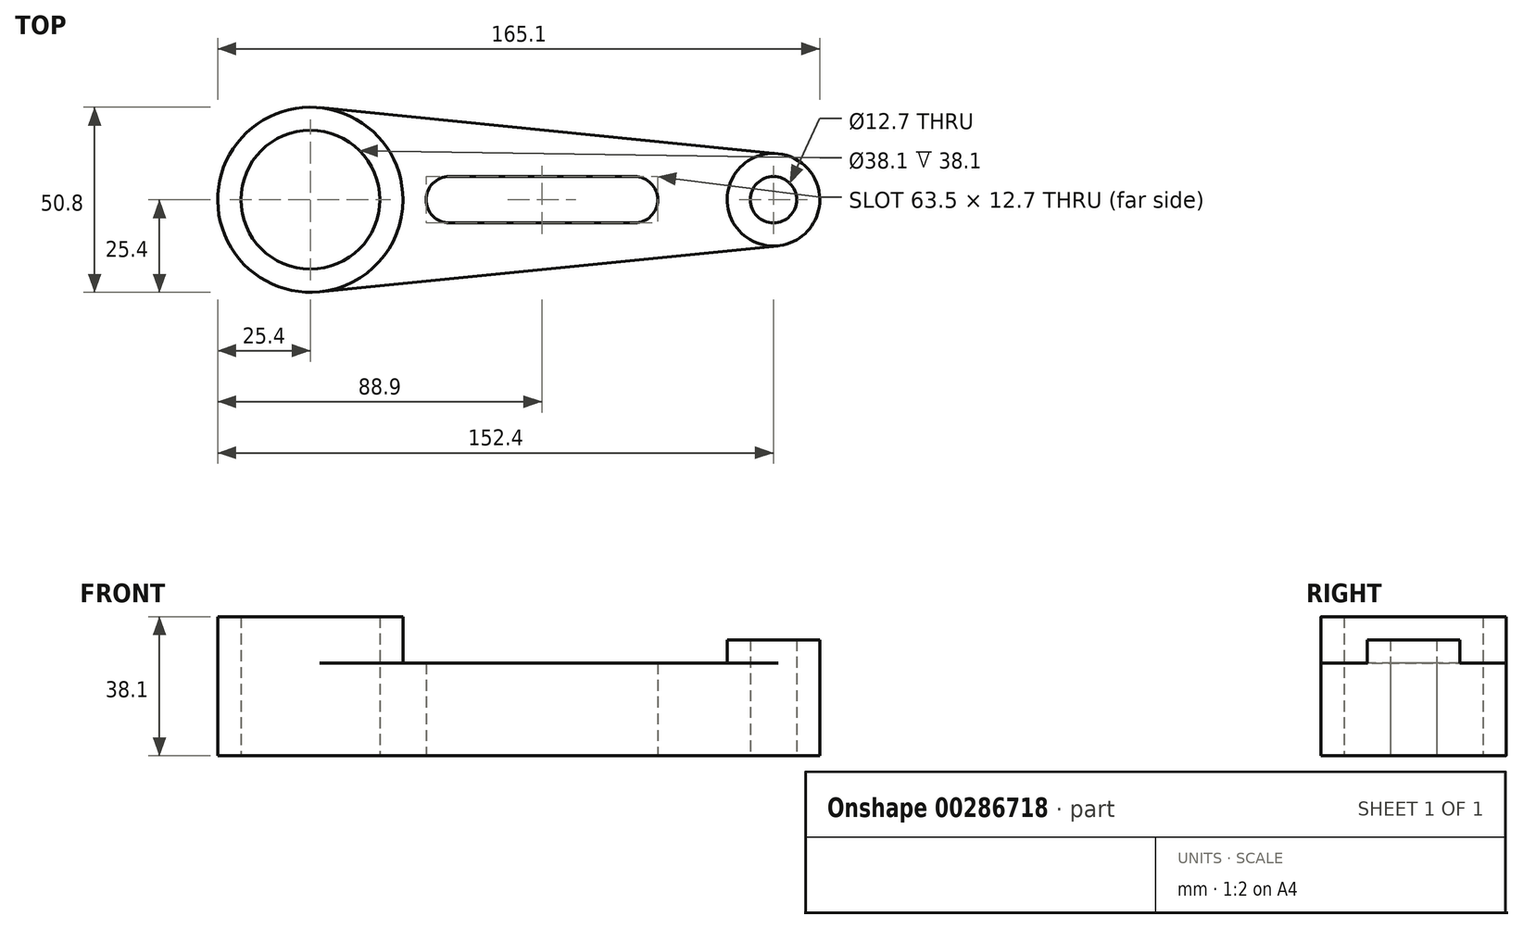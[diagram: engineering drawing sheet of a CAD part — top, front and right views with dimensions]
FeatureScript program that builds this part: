
annotation { "Feature Type Name" : "Feature", "Feature Type Description" : "" }
export const myFeature = defineFeature(function(context is Context, id is Id, definition is map)
    precondition{}
    {
        {
            var Q0;
            Q0=qCreatedBy(makeId("Top.planeOp"),FACE);
            var sketch = newSketch(context, id + "F0", { "sketchPlane" : qUnion([Q0])});
            skCircle(sketch, "E0", {"center": v(-38.1, 0) * mm, "radius": 25.4 * mm});
            skCircle(sketch, "E1", {"center": v(-38.1, 0) * mm, "radius": 19.05 * mm});
            skLineSegment(sketch, "E2", {"start": v(-35.56, 25.27) * mm, "end": v(90.17, 12.64) * mm});
            skLineSegment(sketch, "E3", {"start": v(-35.56, -25.27) * mm, "end": v(90.17, -12.64) * mm});
            skCircle(sketch, "E4", {"center": v(88.9, 0) * mm, "radius": 6.35 * mm});
            skCircle(sketch, "E5", {"center": v(88.9, 0) * mm, "radius": 12.7 * mm});
            skArc(sketch, "E6", {"start": v(0, 6.35) * mm, "mid": v(-6.35, 0) * mm, "end": v(0, -6.35) * mm});
            skArc(sketch, "E7", {"start": v(50.8, -6.35) * mm, "mid": v(57.15, 0) * mm, "end": v(50.8, 6.35) * mm});
            skLineSegment(sketch, "E8", {"start": v(0, 6.35) * mm, "end": v(50.8, 6.35) * mm});
            skLineSegment(sketch, "E9", {"start": v(0, -6.35) * mm, "end": v(50.8, -6.35) * mm});
            skSolve(sketch);
        }
        {
            var Q0;
            Q0=qSketchRegion(id+"F0",true);
            extrude(context, id + "F1", {"entities" : qUnion([Q0]), "depth" : 25.4 * mm});
        }
        {
            var Q0;
            Q0=makeQuery(id+"F0.imprint","IMPRINT",FACE,{"disambiguationData":[TD([[makeQuery(id+"F0.imprint","IMPRINT",EDGE,{"derivedFrom":sQuery(id+"F0.wireOp",EDGE,"E1")}),-1.0]])]});
            extrude(context, id + "F2", {"entities" : qUnion([Q0]), "operationType" : NewBodyOperationType.ADD, "depth" : 38.1 * mm});
        }
        {
            var Q0;
            Q0=makeQuery(id+"F0.imprint","IMPRINT",FACE,{"disambiguationData":[TD([[makeQuery(id+"F0.imprint","IMPRINT",EDGE,{"derivedFrom":sQuery(id+"F0.wireOp",EDGE,"E4")}),-1.0]])]});
            extrude(context, id + "F3", {"entities" : qUnion([Q0]), "operationType" : NewBodyOperationType.ADD, "depth" : 31.75 * mm});
        }
    });
